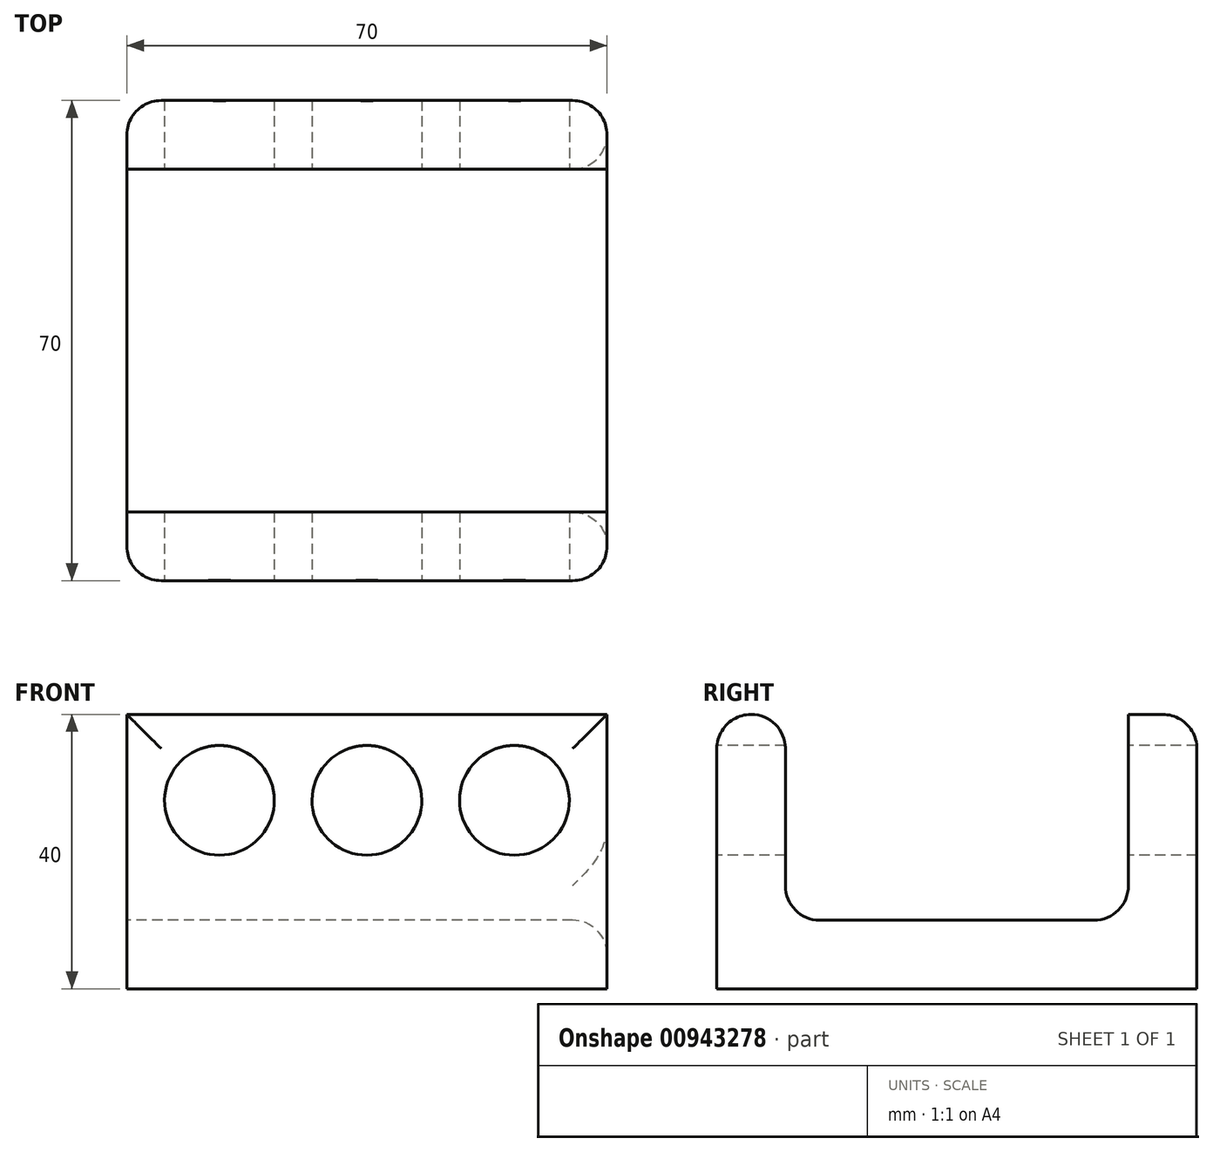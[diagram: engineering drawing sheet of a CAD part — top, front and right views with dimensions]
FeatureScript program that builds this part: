
annotation { "Feature Type Name" : "Feature", "Feature Type Description" : "" }
export const myFeature = defineFeature(function(context is Context, id is Id, definition is map)
    precondition{}
    {
        {
            var Q0;
            Q0=qCreatedBy(makeId("Top.planeOp"),FACE);
            var sketch = newSketch(context, id + "F0", { "sketchPlane" : qUnion([Q0])});
            skLineSegment(sketch, "E0.bottom", {"start": v(35, -35) * mm, "end": v(-35, -35) * mm});
            skLineSegment(sketch, "E0.top", {"start": v(35, 35) * mm, "end": v(-35, 35) * mm});
            skLineSegment(sketch, "E0.left", {"start": v(35, -35) * mm, "end": v(35, 35) * mm});
            skLineSegment(sketch, "E0.right", {"start": v(-35, -35) * mm, "end": v(-35, 35) * mm});
            skPoint(sketch, "E0.middle", {"position": v(0, 0) * mm});
            skSolve(sketch);
        }
        {
            var Q0;
            Q0=makeQuery(id+"F0.imprint","IMPRINT",FACE,{"disambiguationData":[TD([[makeQuery(id+"F0.imprint","IMPRINT",EDGE,{"derivedFrom":sQuery(id+"F0.wireOp",EDGE,"E0.bottom")}),-1.0]])]});
            extrude(context, id + "F1", {"entities" : qUnion([Q0]), "depth" : 40 * mm, "offsetDistance" : 25 * mm});
        }
        {
            var Q0;
            Q0=makeQuery(id+"F1.opExtrude","SWEPT_FACE",FACE,{"disambiguationData":[OSD([sQuery(id+"F0.wireOp",EDGE,"E0.bottom")])]});
            var sketch = newSketch(context, id + "F2", { "sketchPlane" : qUnion([Q0])});
            skLineSegment(sketch, "E1", {"start": v(-35, 27.47) * mm, "end": v(-29.5, 27.47) * mm});
            skLineSegment(sketch, "E2", {"start": v(-29.5, 27.47) * mm, "end": v(-21.5, 27.47) * mm});
            skCircle(sketch, "E3", {"center": v(-21.5, 27.47) * mm, "radius": 8 * mm});
            skLineSegment(sketch, "E4.1.0.0", {"start": v(-13.5, 27.47) * mm, "end": v(-8, 27.47) * mm});
            skCircle(sketch, "E4.1.0.1", {"center": v(0, 27.47) * mm, "radius": 8 * mm});
            skLineSegment(sketch, "E4.2.0.0", {"start": v(8, 27.47) * mm, "end": v(13.5, 27.47) * mm});
            skCircle(sketch, "E4.2.0.1", {"center": v(21.5, 27.47) * mm, "radius": 8 * mm});
            skLineSegment(sketch, "E4.direction1", {"start": v(-35, 27.47) * mm, "end": v(-13.5, 27.47) * mm, "construction": true});
            skSolve(sketch);
        }
        {
            var Q0;
            {var subQ0=sQuery(id+"F2.wireOp",EDGE,"E3");var subQ1=makeQuery(id+"F2.imprint","IMPRINT",VERTEX,{"disambiguationData":[OD(0.0)],"derivedFrom":subQ0});Q0=makeQuery(id+"F2.imprint","IMPRINT",FACE,{"disambiguationData":[TD([[makeQuery(id+"F2.imprint","IMPRINT",EDGE,{"disambiguationData":[TD([[subQ1,1.0]])],"derivedFrom":subQ0}),1.0]])]});}
            var Q1;
            {var subQ0=sQuery(id+"F2.wireOp",EDGE,"e124260f-7d7a-495e-87e1-c11296e3318f.1.0.2");var subQ1=makeQuery(id+"F2.imprint","IMPRINT",VERTEX,{"disambiguationData":[OD(0.0)],"derivedFrom":subQ0});Q1=makeQuery(id+"F2.imprint","IMPRINT",FACE,{"disambiguationData":[TD([[makeQuery(id+"F2.imprint","IMPRINT",EDGE,{"disambiguationData":[TD([[subQ1,1.0]])],"derivedFrom":subQ0}),1.0]])]});}
            var Q2;
            Q2=makeQuery(id+"F2.imprint","IMPRINT",FACE,{"disambiguationData":[TD([[makeQuery(id+"F2.imprint","IMPRINT",EDGE,{"derivedFrom":sQuery(id+"F2.wireOp",EDGE,"e124260f-7d7a-495e-87e1-c11296e3318f.2.0.2")}),1.0]])]});
            var Q3;
            {var subQ0=sQuery(id+"F2.wireOp",EDGE,"E4.1.0.1");var subQ1=makeQuery(id+"F2.imprint","IMPRINT",VERTEX,{"disambiguationData":[OD(0.0)],"derivedFrom":subQ0});Q3=makeQuery(id+"F2.imprint","IMPRINT",FACE,{"disambiguationData":[TD([[makeQuery(id+"F2.imprint","IMPRINT",EDGE,{"disambiguationData":[TD([[subQ1,1.0]])],"derivedFrom":subQ0}),1.0]])]});}
            var Q4;
            Q4=makeQuery(id+"F2.imprint","IMPRINT",FACE,{"disambiguationData":[TD([[makeQuery(id+"F2.imprint","IMPRINT",EDGE,{"derivedFrom":sQuery(id+"F2.wireOp",EDGE,"E4.2.0.1")}),1.0]])]});
            extrude(context, id + "F3", {"entities" : qUnion([Q0, Q1, Q2, Q3, Q4]), "operationType" : NewBodyOperationType.REMOVE, "oppositeDirection" : true, "depth" : 78 * mm, "offsetDistance" : 25 * mm});
        }
        {
            var Q0;
            Q0=makeQuery(id+"F1.opExtrude","SWEPT_FACE",FACE,{"disambiguationData":[OSD([sQuery(id+"F0.wireOp",EDGE,"E0.right")])]});
            var sketch = newSketch(context, id + "F4", { "sketchPlane" : qUnion([Q0])});
            skLineSegment(sketch, "E5", {"start": v(0, 40) * mm, "end": v(0, 17.14) * mm});
            skLineSegment(sketch, "E6", {"start": v(0, 22.62) * mm, "end": v(-25, 22.62) * mm});
            skLineSegment(sketch, "E7", {"start": v(0, 22.62) * mm, "end": v(25, 22.62) * mm});
            skLineSegment(sketch, "E8.bottom", {"start": v(-25, 40) * mm, "end": v(25, 40) * mm});
            skLineSegment(sketch, "E8.top", {"start": v(-25, 10) * mm, "end": v(25, 10) * mm});
            skLineSegment(sketch, "E8.left", {"start": v(-25, 40) * mm, "end": v(-25, 10) * mm});
            skLineSegment(sketch, "E8.right", {"start": v(25, 40) * mm, "end": v(25, 10) * mm});
            skSolve(sketch);
        }
        {
            var Q0;
            {var subQ3=sQuery(id+"F4.wireOp",EDGE,"E6");Q0=makeQuery(id+"F4.imprint","IMPRINT",FACE,{"disambiguationData":[TD([[makeQuery(id+"F4.imprint","IMPRINT",EDGE,{"derivedFrom":subQ3}),-1.0]])]});}
            var Q1;
            {var subQ3=sQuery(id+"F4.wireOp",EDGE,"E7");Q1=makeQuery(id+"F4.imprint","IMPRINT",FACE,{"disambiguationData":[TD([[makeQuery(id+"F4.imprint","IMPRINT",EDGE,{"derivedFrom":subQ3}),1.0]])]});}
            var Q2;
            {var subQ2=sQuery(id+"F4.wireOp",EDGE,"E6");Q2=makeQuery(id+"F4.imprint","IMPRINT",FACE,{"disambiguationData":[TD([[makeQuery(id+"F4.imprint","IMPRINT",EDGE,{"derivedFrom":subQ2}),1.0]])]});}
            extrude(context, id + "F5", {"entities" : qUnion([Q0, Q1, Q2]), "operationType" : NewBodyOperationType.REMOVE, "oppositeDirection" : true, "depth" : 72.2 * mm, "offsetDistance" : 25 * mm});
        }
        {
            var Q0;
            Q0=makeQuery(id+"F5.boolean.opBoolean","COPY",EDGE,{"derivedFrom":makeQuery(id+"F5.opExtrude","SWEPT_EDGE",EDGE,{"disambiguationData":[OSD([sQuery(id+"F4.wireOp",EDGE,"E8.top"),sQuery(id+"F4.wireOp",EDGE,"E8.left")])]})});
            var Q1;
            Q1=makeQuery(id+"F5.boolean.opBoolean","COPY",EDGE,{"derivedFrom":makeQuery(id+"F5.opExtrude","SWEPT_EDGE",EDGE,{"disambiguationData":[OSD([sQuery(id+"F4.wireOp",EDGE,"E8.top"),sQuery(id+"F4.wireOp",EDGE,"E8.right")])]})});
            var Q2;
            Q2=makeQuery(id+"F5.boolean.opBoolean","INTERSECT",EDGE,{"derivedFrom":[makeQuery(id+"F1.opExtrude","SWEPT_FACE",FACE,{"disambiguationData":[OSD([sQuery(id+"F0.wireOp",EDGE,"E0.left")])]}),makeQuery(id+"F5.opExtrude","SWEPT_FACE",FACE,{"disambiguationData":[OSD([sQuery(id+"F4.wireOp",EDGE,"E8.top")])]})]});
            var Q3;
            Q3=makeQuery(id+"F1.opExtrude","SWEPT_EDGE",EDGE,{"disambiguationData":[OSD([sQuery(id+"F0.wireOp",EDGE,"E0.bottom"),sQuery(id+"F0.wireOp",EDGE,"E0.left")])]});
            var Q4;
            Q4=makeQuery(id+"F1.opExtrude","SWEPT_EDGE",EDGE,{"disambiguationData":[OSD([sQuery(id+"F0.wireOp",EDGE,"E0.top"),sQuery(id+"F0.wireOp",EDGE,"E0.left")])]});
            var Q5;
            Q5=makeQuery(id+"F1.opExtrude","SWEPT_EDGE",EDGE,{"disambiguationData":[OSD([sQuery(id+"F0.wireOp",EDGE,"E0.top"),sQuery(id+"F0.wireOp",EDGE,"E0.right")])]});
            var Q6;
            Q6=makeQuery(id+"F5.boolean.opBoolean","COPY",EDGE,{"derivedFrom":makeQuery(id+"F5.opExtrude","CAP_EDGE",EDGE,{"disambiguationData":[OSD([sQuery(id+"F4.wireOp",EDGE,"E8.left")])],"isStart":true})});
            var Q7;
            Q7=makeQuery(id+"F1.opExtrude","SWEPT_EDGE",EDGE,{"disambiguationData":[OSD([sQuery(id+"F0.wireOp",EDGE,"E0.bottom"),sQuery(id+"F0.wireOp",EDGE,"E0.right")])]});
            var Q8;
            Q8=makeQuery(id+"F5.boolean.opBoolean","COPY",EDGE,{"derivedFrom":makeQuery(id+"F5.opExtrude","SWEPT_EDGE",EDGE,{"disambiguationData":[OSD([sQuery(id+"F0.wireOp",EDGE,"E0.right"),sQuery(id+"F4.wireOp",EDGE,"E8.bottom"),sQuery(id+"F4.wireOp",EDGE,"E8.right")])]})});
            var Q9;
            Q9=makeQuery(id+"F1.opExtrude","CAP_EDGE",EDGE,{"disambiguationData":[OSD([sQuery(id+"F0.wireOp",EDGE,"E0.bottom")])],"isStart":false});
            var Q10;
            Q10=makeQuery(id+"F1.opExtrude","CAP_EDGE",EDGE,{"disambiguationData":[OSD([sQuery(id+"F0.wireOp",EDGE,"E0.top")])],"isStart":false});
            var Q11;
            Q11=makeQuery(id+"F5.boolean.opBoolean","COPY",EDGE,{"derivedFrom":makeQuery(id+"F5.opExtrude","SWEPT_EDGE",EDGE,{"disambiguationData":[OSD([sQuery(id+"F0.wireOp",EDGE,"E0.right"),sQuery(id+"F4.wireOp",EDGE,"E8.bottom"),sQuery(id+"F4.wireOp",EDGE,"E8.left")])]})});
            fillet(context, id + "F6", {"entities" : qUnion([Q0, Q1, Q2, Q3, Q4, Q5, Q6, Q7, Q8, Q9, Q10, Q11]), "radius" : 5 * mm, "tangentPropagation" : true, "allowEdgeOverflow" : false});
        }
    });
